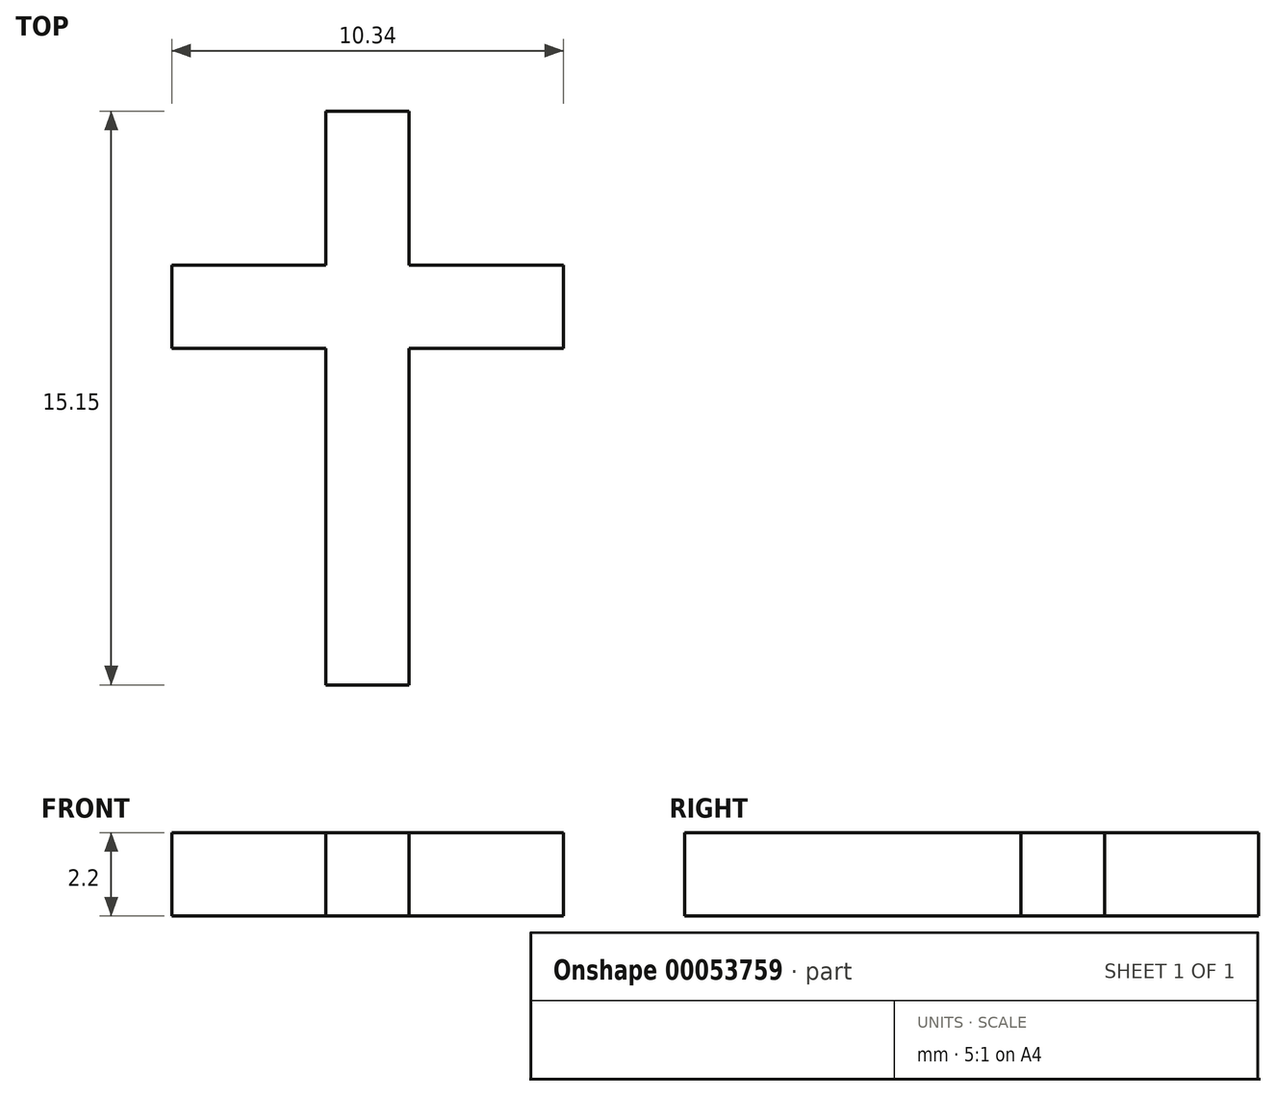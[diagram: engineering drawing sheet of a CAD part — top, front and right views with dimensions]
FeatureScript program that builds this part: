
annotation { "Feature Type Name" : "Feature", "Feature Type Description" : "" }
export const myFeature = defineFeature(function(context is Context, id is Id, definition is map)
    precondition{}
    {
        {
            var Q0;
            Q0=qCreatedBy(makeId("Top.planeOp"),FACE);
            var sketch = newSketch(context, id + "F0", { "sketchPlane" : qUnion([Q0])});
            skLineSegment(sketch, "E0.bottom", {"start": v(-1.1, 0) * mm, "end": v(1.1, 0) * mm});
            skLineSegment(sketch, "E0.top", {"start": v(-1.1, 15.15) * mm, "end": v(1.1, 15.15) * mm});
            skLineSegment(sketch, "E0.left", {"start": v(-1.1, 0) * mm, "end": v(-1.1, 15.15) * mm});
            skLineSegment(sketch, "E0.right", {"start": v(1.1, 0) * mm, "end": v(1.1, 15.15) * mm});
            skLineSegment(sketch, "E1.bottom", {"start": v(-5.17, 11.09) * mm, "end": v(5.17, 11.09) * mm});
            skLineSegment(sketch, "E1.top", {"start": v(-5.17, 8.89) * mm, "end": v(5.17, 8.89) * mm});
            skLineSegment(sketch, "E1.left", {"start": v(-5.17, 11.09) * mm, "end": v(-5.17, 8.89) * mm});
            skLineSegment(sketch, "E1.right", {"start": v(5.17, 11.09) * mm, "end": v(5.17, 8.89) * mm});
            skLineSegment(sketch, "E2", {"start": v(-5.17, 11.09) * mm, "end": v(-1.1, 15.15) * mm, "construction": true});
            skSolve(sketch);
        }
        {
            var Q0;
            Q0 = qSketchRegion(id + "F0", true);
            extrude(context, id + "F1", {"entities" : qUnion([Q0]), "depth" : 2.2 * mm});
        }
    });
